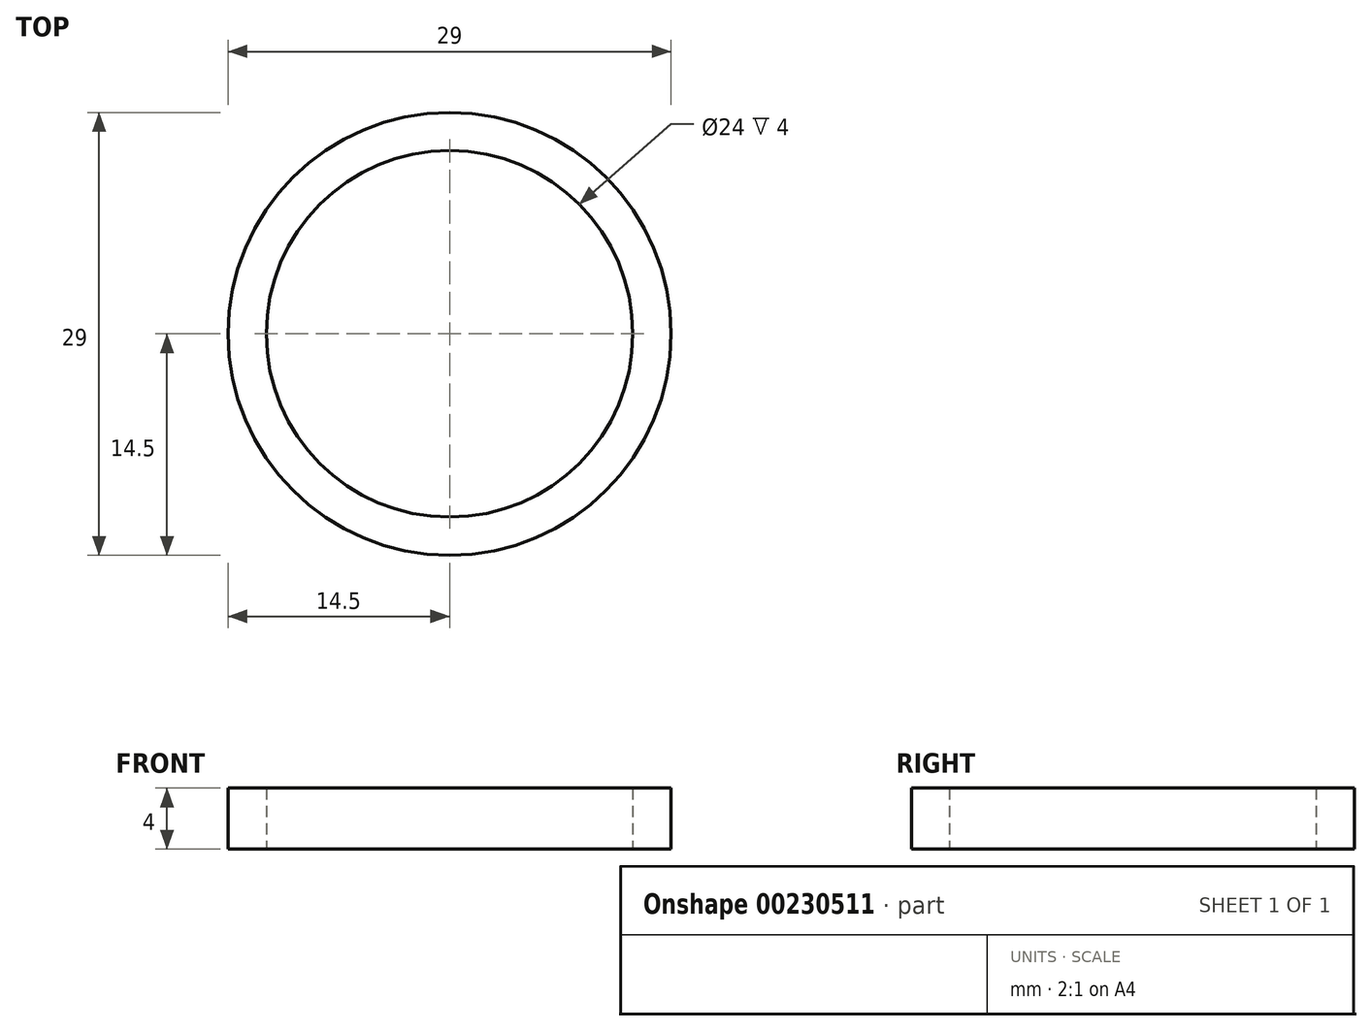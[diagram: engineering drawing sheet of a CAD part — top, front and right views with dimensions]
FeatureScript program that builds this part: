
annotation { "Feature Type Name" : "Feature", "Feature Type Description" : "" }
export const myFeature = defineFeature(function(context is Context, id is Id, definition is map)
    precondition{}
    {
        {
            var Q0;
            Q0=qCreatedBy(makeId("Top.planeOp"),FACE);
            var sketch = newSketch(context, id + "F0", { "sketchPlane" : qUnion([Q0])});
            skCircle(sketch, "E0", {"center": v(0, 0) * mm, "radius": 12 * mm});
            skCircle(sketch, "E1", {"center": v(0, 0) * mm, "radius": 14.5 * mm});
            skSolve(sketch);
        }
        {
            var Q0;
            Q0=makeQuery(id+"F0.imprint","IMPRINT",FACE,{"disambiguationData":[TD([[makeQuery(id+"F0.imprint","IMPRINT",EDGE,{"derivedFrom":sQuery(id+"F0.wireOp",EDGE,"E0")}),-1.0]])]});
            extrude(context, id + "F1", {"entities" : qUnion([Q0]), "depth" : 4 * mm});
        }
    });
